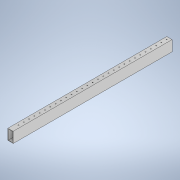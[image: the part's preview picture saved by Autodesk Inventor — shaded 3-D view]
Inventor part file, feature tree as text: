
AUTODESK INVENTOR PART (.ipt)
format: ipt  version: 2020 (Build 240168000, 168)  size: 188,928 bytes
history: native  units: in
note: dims shown in document units (in); Inventor stores cm internally (conversion verified against a paired STEP export)
features: extrude x2, sketch x2
ambient origin geometry x8: Origin, YZ Plane, XZ Plane, XY Plane, X Axis, Y Axis, Z Axis, Center Point
bodies: Solid1 (feature_tree)
feature tree (4):
  extrude  "Extrusion1"  Depth=2.0in
  extrude  "Extrusion2"  Depth=30.0in TaperAngle=0.0deg
  sketch  "Sketch1"  dims[d0=1.0in d1=2.0in]
  sketch  "Sketch2"  dims[d2=0.1in d3=30.0in d4=0.0in d5=0.1562in d6=0.5in d7=0.5in d8=12.9921in d10=1.0in d11=0.3937in d13=1.0in d15=22.0in d16=0.0in]
